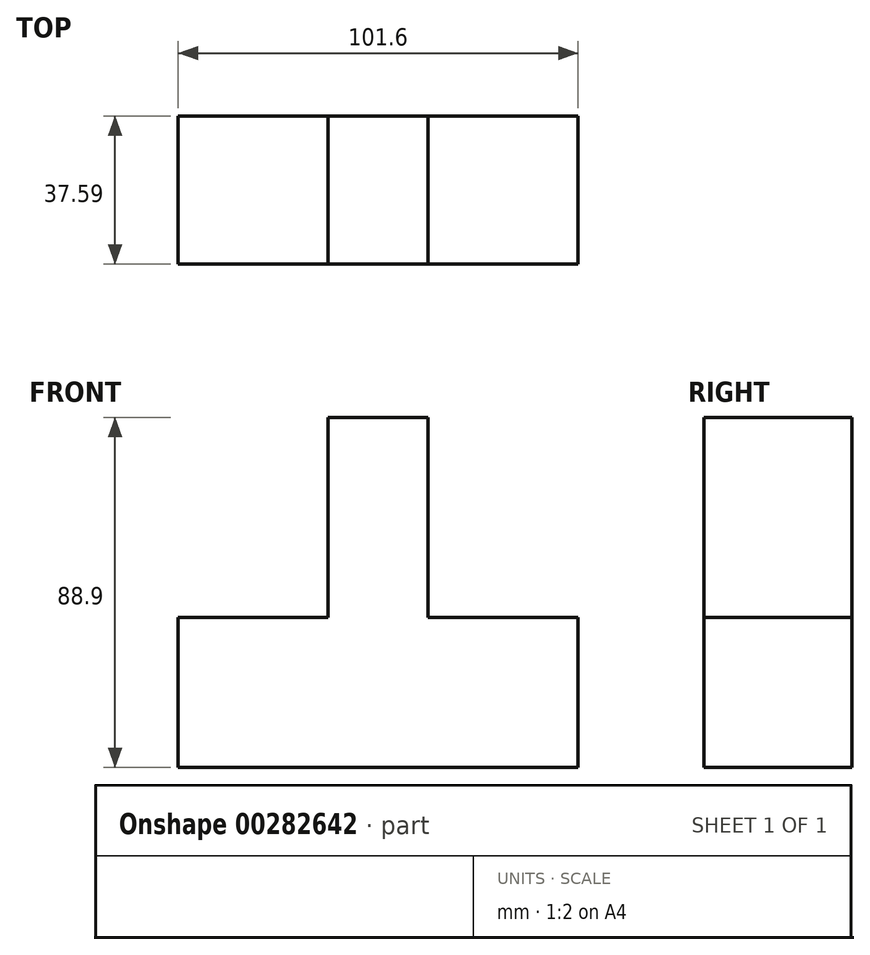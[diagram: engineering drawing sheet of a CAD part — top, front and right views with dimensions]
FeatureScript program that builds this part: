
annotation { "Feature Type Name" : "Feature", "Feature Type Description" : "" }
export const myFeature = defineFeature(function(context is Context, id is Id, definition is map)
    precondition{}
    {
        {
            var Q0;
            Q0=qCreatedBy(makeId("Front.planeOp"),FACE);
            var sketch = newSketch(context, id + "F0", { "sketchPlane" : qUnion([Q0])});
            skLineSegment(sketch, "E0", {"start": v(-65.3, -56.1) * mm, "end": v(36.3, -56.1) * mm});
            skLineSegment(sketch, "E1", {"start": v(36.3, -56.1) * mm, "end": v(36.3, -18) * mm});
            skLineSegment(sketch, "E2", {"start": v(-65.3, -56.1) * mm, "end": v(-65.3, -18) * mm});
            skLineSegment(sketch, "E3", {"start": v(-65.3, -18) * mm, "end": v(-27.2, -18) * mm});
            skLineSegment(sketch, "E4", {"start": v(36.3, -18) * mm, "end": v(-1.8, -18) * mm});
            skLineSegment(sketch, "E5", {"start": v(-1.8, -18) * mm, "end": v(-1.8, 32.8) * mm});
            skLineSegment(sketch, "E6", {"start": v(-27.2, -18) * mm, "end": v(-27.2, 32.8) * mm});
            skLineSegment(sketch, "E7", {"start": v(-27.2, 32.8) * mm, "end": v(-1.8, 32.8) * mm});
            skSolve(sketch);
        }
        {
            var Q0;
            Q0 = qSketchRegion(id + "F0", true);
            extrude(context, id + "F1", {"entities" : qUnion([Q0]), "depth" : 37.6 * mm});
        }
    });
